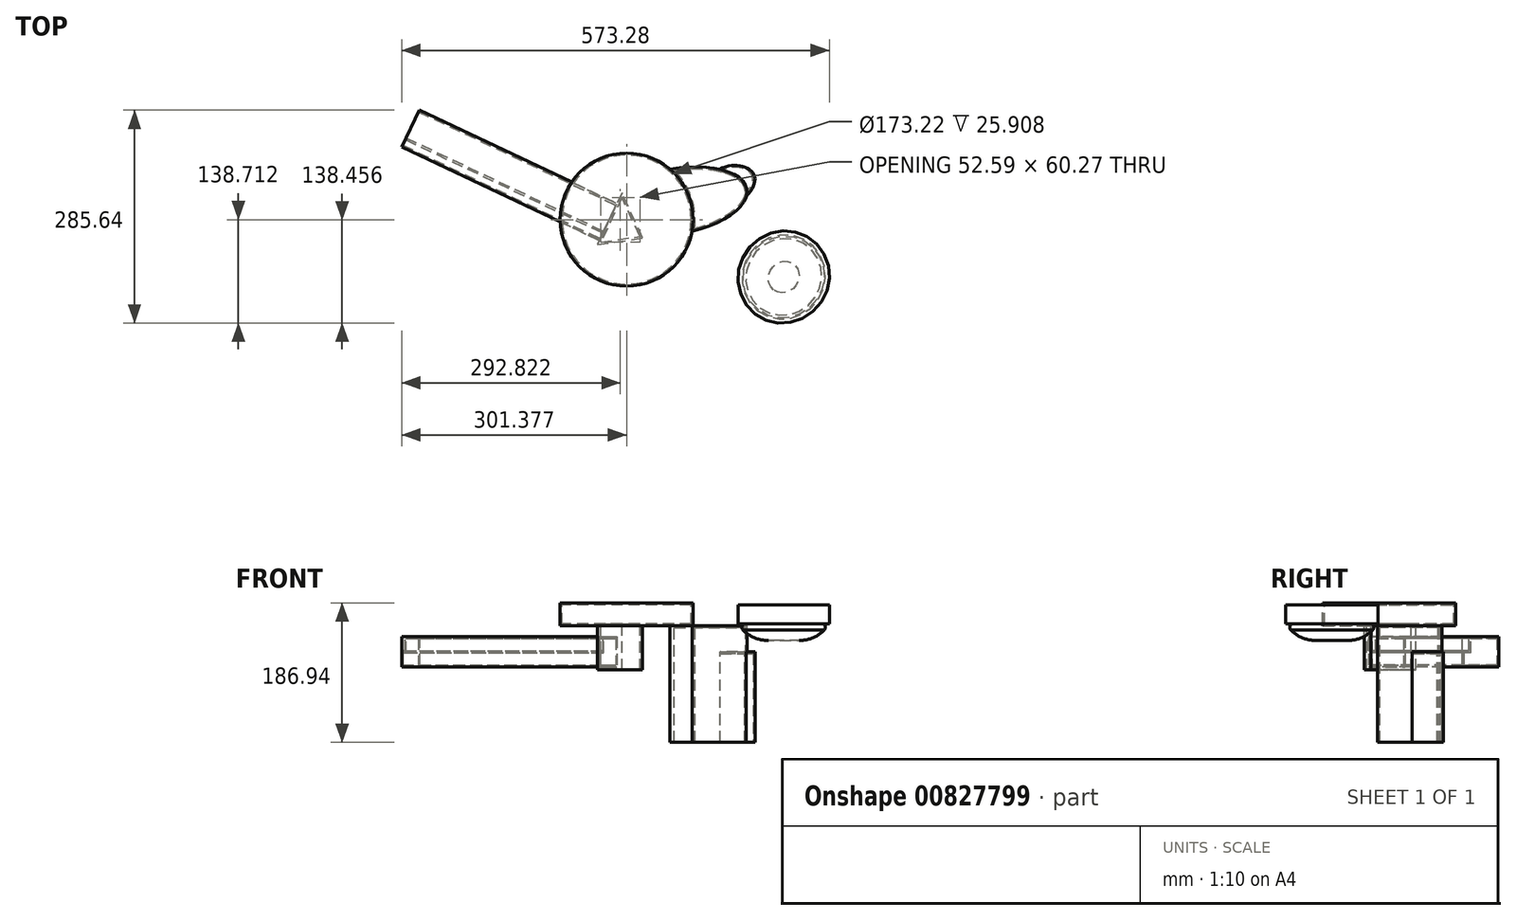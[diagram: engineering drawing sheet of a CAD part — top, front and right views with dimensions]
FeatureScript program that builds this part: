
annotation { "Feature Type Name" : "Feature", "Feature Type Description" : "" }
export const myFeature = defineFeature(function(context is Context, id is Id, definition is map)
    precondition{}
    {
        {
            var Q0;
            Q0=qCreatedBy(makeId("Top.planeOp"),FACE);
            var sketch = newSketch(context, id + "F0", { "sketchPlane" : qUnion([Q0])});
            skCircle(sketch, "E0", {"center": v(45.57, -108) * mm, "radius": 89.15 * mm});
            skPoint(sketch, "E0.first.point", {"position": v(117.79, -55.73) * mm});
            skPoint(sketch, "E0.second.point", {"position": v(-14.25, -41.9) * mm});
            skPoint(sketch, "E0.third.point", {"position": v(-14.61, -42.22) * mm});
            skSolve(sketch);
        }
        {
            var Q0;
            Q0=makeQuery(id+"F0.imprint","IMPRINT",FACE,{"disambiguationData":[TD([[makeQuery(id+"F0.imprint","IMPRINT",EDGE,{"derivedFrom":sQuery(id+"F0.wireOp",EDGE,"E0")}),1.0]])]});
            extrude(context, id + "F1", {"entities" : qUnion([Q0]), "oppositeDirection" : true, "depth" : 30.99 * mm, "offsetDistance" : 25.4 * mm});
        }
        {
            var Q0;
            Q0=makeQuery(id+"F1.opExtrude","CAP_FACE",FACE,{"disambiguationData":[OSD([sQuery(id+"F0.wireOp",EDGE,"E0")])],"isStart":false});
            var sketch = newSketch(context, id + "F2", { "sketchPlane" : qUnion([Q0])});
            skEllipse(sketch, "E1", {"center": v(113.26, 83.24) * mm, "majorRadius": 94.84 * mm, "minorRadius": 43.7 * mm, "majorAxis": v(-0.99, 0.17)});
            skSolve(sketch);
        }
        {
            var Q0;
            {var subQ0=sQuery(id+"F2.wireOp",EDGE,"E1");var subQ1=makeQuery(id+"F1.opExtrude","CAP_EDGE",EDGE,{"disambiguationData":[OSD([sQuery(id+"F0.wireOp",EDGE,"E0")])],"isStart":false});var subQ2=makeQuery(id+"F2.imprint","INTERSECT",VERTEX,{"disambiguationData":[OD(0.0)],"derivedFrom":[subQ1,subQ0]});Q0=makeQuery(id+"F2.imprint","IMPRINT",FACE,{"disambiguationData":[TD([[makeQuery(id+"F2.imprint","IMPRINT",EDGE,{"disambiguationData":[TD([[subQ2,1.0]])],"derivedFrom":subQ0}),1.0]])]});}
            extrude(context, id + "F3", {"entities" : qUnion([Q0]), "depth" : 34.8 * mm, "offsetDistance" : 25.4 * mm});
        }
        {
            var Q0;
            Q0=makeQuery(id+"F1.opExtrude","CAP_FACE",FACE,{"disambiguationData":[OSD([sQuery(id+"F0.wireOp",EDGE,"E0")])],"isStart":false});
            var sketch = newSketch(context, id + "F4", { "sketchPlane" : qUnion([Q0])});
            skLineSegment(sketch, "E2", {"start": v(67.03, 132.51) * mm, "end": v(39.26, 72.11) * mm});
            skLineSegment(sketch, "E3", {"start": v(39.26, 72.11) * mm, "end": v(6.38, 141.6) * mm});
            skLineSegment(sketch, "E4", {"start": v(6.38, 141.6) * mm, "end": v(67.03, 132.51) * mm});
            skSolve(sketch);
        }
        {
            var Q0;
            Q0=makeQuery(id+"F4.imprint","IMPRINT",FACE,{"disambiguationData":[TD([[makeQuery(id+"F4.imprint","IMPRINT",EDGE,{"derivedFrom":sQuery(id+"F4.wireOp",EDGE,"E2")}),-1.0]])]});
            extrude(context, id + "F5", {"entities" : qUnion([Q0]), "operationType" : NewBodyOperationType.ADD, "depth" : 58.93 * mm, "offsetDistance" : 25.4 * mm});
        }
        {
            var Q0;
            Q0=makeQuery(id+"F5.opExtrude","SWEPT_FACE",FACE,{"disambiguationData":[OSD([sQuery(id+"F4.wireOp",EDGE,"E4")])]});
            var sketch = newSketch(context, id + "F6", { "sketchPlane" : qUnion([Q0])});
            skArc(sketch, "E5", {"start": v(-14.7, -124.47) * mm, "mid": v(82, -178.1) * mm, "end": v(36.67, -77.25) * mm});
            skSolve(sketch);
        }
        {
            var Q0;
            Q0=sQuery(id+"F6.wireOp",EDGE,"E5");
            extrude(context, id + "F7", {"bodyType" : ToolBodyType.SURFACE, "surfaceEntities" : qUnion([Q0]), "depth" : 68.58 * mm, "offsetDistance" : 25.4 * mm});
        }
        {
            var Q0;
            Q0=makeQuery(id+"F3.opExtrude","CAP_FACE",FACE,{"disambiguationData":[OSD([sQuery(id+"F0.wireOp",EDGE,"E0"),sQuery(id+"F2.wireOp",EDGE,"E1")])],"isStart":false});
            var sketch = newSketch(context, id + "F8", { "sketchPlane" : qUnion([Q0])});
            skFitSpline(sketch, "E6", {"points": [v(170.59, 40.54) * mm, v(146.1, 108.11) * mm, v(217.58, 55.36) * mm, v(170.59, 40.54) * mm]});
            skSolve(sketch);
        }
        {
            var Q0;
            {var subQ0=sQuery(id+"F8.wireOp",EDGE,"E6");var subQ1=makeQuery(id+"F3.opExtrude","CAP_EDGE",EDGE,{"disambiguationData":[OSD([sQuery(id+"F2.wireOp",EDGE,"E1")])],"isStart":false});var subQ2=makeQuery(id+"F8.imprint","INTERSECT",VERTEX,{"disambiguationData":[OD(0.0)],"derivedFrom":[subQ1,subQ0]});Q0=makeQuery(id+"F8.imprint","IMPRINT",FACE,{"disambiguationData":[TD([[makeQuery(id+"F8.imprint","IMPRINT",EDGE,{"disambiguationData":[TD([[subQ2,-1.0]])],"derivedFrom":subQ0}),-1.0]])]});}
            var Q1;
            {var subQ0=sQuery(id+"F8.wireOp",EDGE,"E6");var subQ1=makeQuery(id+"F3.opExtrude","CAP_EDGE",EDGE,{"disambiguationData":[OSD([sQuery(id+"F2.wireOp",EDGE,"E1")])],"isStart":false});var subQ2=makeQuery(id+"F8.imprint","INTERSECT",VERTEX,{"disambiguationData":[OD(0.0)],"derivedFrom":[subQ1,subQ0]});Q1=makeQuery(id+"F8.imprint","IMPRINT",FACE,{"disambiguationData":[TD([[makeQuery(id+"F8.imprint","IMPRINT",EDGE,{"disambiguationData":[TD([[subQ2,1.0]])],"derivedFrom":subQ0}),-1.0]])]});}
            var Q2;
            Q2=makeQuery(id+"F3.opExtrude","CAP_FACE",FACE,{"disambiguationData":[OSD([sQuery(id+"F0.wireOp",EDGE,"E0"),sQuery(id+"F2.wireOp",EDGE,"E1")])],"isStart":false});
            extrude(context, id + "F9", {"entities" : qUnion([Q0, Q1, Q2]), "operationType" : NewBodyOperationType.ADD, "depth" : 121.16 * mm, "offsetDistance" : 25.4 * mm});
        }
        {
            var Q0;
            Q0=makeQuery(id+"F5.opExtrude","CAP_FACE",FACE,{"disambiguationData":[OSD([sQuery(id+"F4.wireOp",EDGE,"E2"),sQuery(id+"F4.wireOp",EDGE,"E3"),sQuery(id+"F4.wireOp",EDGE,"E4")])],"isStart":false});
            shell(context, id + "F10", {"entities" : qUnion([Q0]), "thickness" : 2.54 * mm});
        }
        {
            var Q0;
            Q0=makeQuery(id+"F9.boolean.opBoolean","MERGE",FACE,{"derivedFrom":[makeQuery(id+"F9.opExtrude","CAP_FACE",FACE,{"disambiguationData":[OSD([sQuery(id+"F0.wireOp",EDGE,"E0"),sQuery(id+"F2.wireOp",EDGE,"E1")])],"isStart":false}),makeQuery(id+"F9.opExtrude","CAP_FACE",FACE,{"disambiguationData":[OSD([sQuery(id+"F8.wireOp",EDGE,"E6")])],"isStart":false})]});
            shell(context, id + "F11", {"entities" : qUnion([Q0]), "thickness" : 2.54 * mm});
        }
        {
            var Q0;
            Q0=makeQuery(id+"F5.opExtrude","SWEPT_FACE",FACE,{"disambiguationData":[OSD([sQuery(id+"F4.wireOp",EDGE,"E3")])]});
            var sketch = newSketch(context, id + "F12", { "sketchPlane" : qUnion([Q0])});
            skLineSegment(sketch, "E7.bottom", {"start": v(108, -64.42) * mm, "end": v(118.34, -64.42) * mm});
            skLineSegment(sketch, "E7.top", {"start": v(108, -46.02) * mm, "end": v(118.34, -46.02) * mm});
            skLineSegment(sketch, "E7.left", {"start": v(108, -64.42) * mm, "end": v(108, -46.02) * mm});
            skLineSegment(sketch, "E7.right", {"start": v(118.34, -64.42) * mm, "end": v(118.34, -46.02) * mm});
            skLineSegment(sketch, "E8.bottom", {"start": v(118.79, -45.55) * mm, "end": v(64.21, -45.55) * mm});
            skLineSegment(sketch, "E8.top", {"start": v(118.79, -85.73) * mm, "end": v(64.21, -85.73) * mm});
            skLineSegment(sketch, "E8.left", {"start": v(118.79, -45.55) * mm, "end": v(118.79, -85.73) * mm});
            skLineSegment(sketch, "E8.right", {"start": v(64.21, -45.55) * mm, "end": v(64.21, -85.73) * mm});
            skSolve(sketch);
        }
        {
            var Q0;
            Q0 = qSketchRegion(id + "F12", true);
            extrude(context, id + "F13", {"entities" : qUnion([Q0]), "operationType" : NewBodyOperationType.ADD, "depth" : 293.12 * mm, "offsetDistance" : 25.4 * mm});
        }
        {
            var Q0;
            Q0=makeQuery(id+"F13.opExtrude","CAP_FACE",FACE,{"disambiguationData":[OSD([sQuery(id+"F12.wireOp",EDGE,"E7.bottom"),sQuery(id+"F12.wireOp",EDGE,"E7.top"),sQuery(id+"F12.wireOp",EDGE,"E7.left"),sQuery(id+"F12.wireOp",EDGE,"E7.right"),sQuery(id+"F12.wireOp",EDGE,"E8.bottom"),sQuery(id+"F12.wireOp",EDGE,"E8.top"),sQuery(id+"F12.wireOp",EDGE,"E8.left"),sQuery(id+"F12.wireOp",EDGE,"E8.right")])],"isStart":false});
            var Q1;
            Q1=makeQuery(id+"F1.opExtrude","CAP_FACE",FACE,{"disambiguationData":[OSD([sQuery(id+"F0.wireOp",EDGE,"E0")])],"isStart":false});
            shell(context, id + "F14", {"entities" : qUnion([Q0, Q1]), "thickness" : 2.54 * mm});
        }
        {
            var Q0;
            {var subQ0=sQuery(id+"F0.wireOp",EDGE,"E0");Q0=makeQuery(id+"F10.opShell","OFFSET_FACE",FACE,{"disambiguationData":[OSD([subQ0]),TDD([makeQuery(id+"F1.opExtrude","CAP_FACE",FACE,{"disambiguationData":[OSD([subQ0])],"isStart":true})])]});}
            var sketch = newSketch(context, id + "F15", { "sketchPlane" : qUnion([Q0])});
            skEllipse(sketch, "E9", {"center": v(256.12, 184.83) * mm, "majorRadius": 62.61 * mm, "minorRadius": 60.6 * mm, "majorAxis": v(-0.6, 0.8)});
            skSolve(sketch);
        }
        {
            var Q0;
            Q0 = qSketchRegion(id + "F15", true);
            extrude(context, id + "F16", {"entities" : qUnion([Q0]), "depth" : 25.4 * mm, "offsetDistance" : 25.4 * mm});
        }
        {
            var Q0;
            Q0=makeQuery(id+"F16.opExtrude","CAP_FACE",FACE,{"disambiguationData":[OSD([sQuery(id+"F15.wireOp",EDGE,"E9")])],"isStart":false});
            extrude(context, id + "F17", {"entities" : qUnion([Q0]), "depth" : 22.6 * mm, "offsetDistance" : 25.4 * mm});
        }
        {
            var Q0;
            Q0=makeQuery(id+"F17.opExtrude","CAP_EDGE",EDGE,{"disambiguationData":[OSD([sQuery(id+"F15.wireOp",EDGE,"E9")])],"isStart":false});
            fillet(context, id + "F18", {"entities" : qUnion([Q0]), "radius" : 47.83 * mm, "tangentPropagation" : true, "allowEdgeOverflow" : false});
        }
        {
            var Q0;
            Q0=makeQuery(id+"F18.opFillet","BLEND_FACE",FACE,{"disambiguationData":[OSD([sQuery(id+"F15.wireOp",EDGE,"E9")])]});
            fillet(context, id + "F19", {"entities" : qUnion([Q0]), "radius" : 5.08 * mm, "tangentPropagation" : true, "allowEdgeOverflow" : false});
        }
    });
